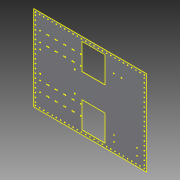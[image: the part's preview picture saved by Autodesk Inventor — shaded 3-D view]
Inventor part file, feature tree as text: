
AUTODESK INVENTOR PART (.ipt)
format: ipt  version: 2014 SP1 (Build 180222100, 222)  size: 615,424 bytes
history: native  units: in
note: dims shown in document units (in); Inventor stores cm internally (conversion verified against a paired STEP export)
features: reference x81, sketch x8, other x7, sheet_metal_op x5, pattern_linear x2, projected_geometry x1
ambient origin geometry x8: Origin, YZ Plane, XZ Plane, XY Plane, X Axis, Y Axis, Z Axis, Center Point
bodies: Solid1 (feature_tree)
feature tree (104):
  sheet_metal_op  "Face1"
  pattern_linear  "Rectangular Pattern2"  Count1=27 Spacing1=1.0in
  pattern_linear  "Rectangular Pattern5"  Spacing1=1.0in  [1 undecoded]
  sheet_metal_op  "Face4"
  sheet_metal_op  "Face5"
  sketch  "Sketch22"  dims[d18=0.0in d19=10.6299in d21=1.0in d23=1.0in d24=1.0in d65=0.0625in d66=0.0in d78=11.55in d79=5.5in d80=11.55in d97=0.0625in d98=0.0in d99=7.4803in d101=1.0in d102=0.7874in d104=26.0in d105=0.0625in d106=0.0in d107=1.0in d109=1.8325in d110=2.5in d111=0.125in d112=3.937in d114=1.8325in d115=3.937in d117=2.5in d122=0.0625in d123=0.0625in d124=0.0312in d125=0.125in d126=0.0625in d127=0.0625in d128=0.0625in d129=0.0312in d130=0.125in d131=0.0625in]
  sketch  "Sketch1"  dims[d0=27.0in]
  other  "Plate1"
  sketch  "Sketch2"  dims[d1=20.325in]
  sketch  "Sketch4"  dims[d2=0.0625in]
  reference  "Reference4"
  reference  "Reference5"
  sketch  "Sketch12"  dims[d4=7.25in]
  reference  "Reference10"
  reference  "Reference11"
  sketch  "Sketch16"  dims[d5=5.5in]
  reference  "Reference12"
  reference  "Reference13"
  reference  "Reference14"
  reference  "Reference15"
  reference  "Reference16"
  reference  "Reference17"
  reference  "Reference18"
  reference  "Reference19"
  reference  "Reference20"
  reference  "Reference21"
  reference  "Reference22"
  reference  "Reference23"
  reference  "Reference24"
  reference  "Reference25"
  reference  "Reference26"
  reference  "Reference27"
  reference  "Reference28"
  reference  "Reference29"
  reference  "Reference30"
  reference  "Reference31"
  reference  "Reference32"
  reference  "Reference33"
  reference  "Reference34"
  reference  "Reference35"
  reference  "Reference36"
  reference  "Reference37"
  reference  "Reference38"
  reference  "Reference39"
  reference  "Reference40"
  reference  "Reference41"
  reference  "Reference42"
  reference  "Reference43"
  reference  "Reference44"
  reference  "Reference45"
  reference  "Reference46"
  projected_geometry  "Projected Loop1"
  reference  "Reference47"
  reference  "Reference48"
  reference  "Reference49"
  reference  "Reference50"
  reference  "Reference51"
  reference  "Reference52"
  reference  "Reference53"
  reference  "Reference54"
  reference  "Reference55"
  reference  "Reference56"
  reference  "Reference57"
  reference  "Reference58"
  reference  "Reference59"
  reference  "Reference60"
  reference  "Reference61"
  reference  "Reference62"
  reference  "Reference63"
  reference  "Reference64"
  reference  "Reference65"
  reference  "Reference66"
  reference  "Reference67"
  reference  "Reference68"
  reference  "Reference69"
  reference  "Reference70"
  reference  "Reference71"
  reference  "Reference72"
  reference  "Reference73"
  reference  "Reference74"
  reference  "Reference75"
  reference  "Reference76"
  reference  "Reference77"
  reference  "Reference78"
  reference  "Reference79"
  reference  "Reference80"
  reference  "Reference81"
  reference  "Reference82"
  reference  "Reference83"
  reference  "Reference84"
  reference  "Reference85"
  reference  "Reference86"
  reference  "Reference87"
  reference  "Reference88"
  sketch  "Sketch19"  dims[d6=7.25in]
  other  "Plate4"
  sheet_metal_op  "Bend3"
  sketch  "Sketch21"  dims[d17=0.0625in]
  other  "Plate5"
  sheet_metal_op  "Bend4"
  other  "Cut3"
  other  "Cut6"
  other  "Cut8"
  other  "Cut9"
note: 1 required parameter value undecoded (feature->parameter linkage not recoverable at this tier; creation-order binding heuristic only, values carry confidence <= 0.55)
